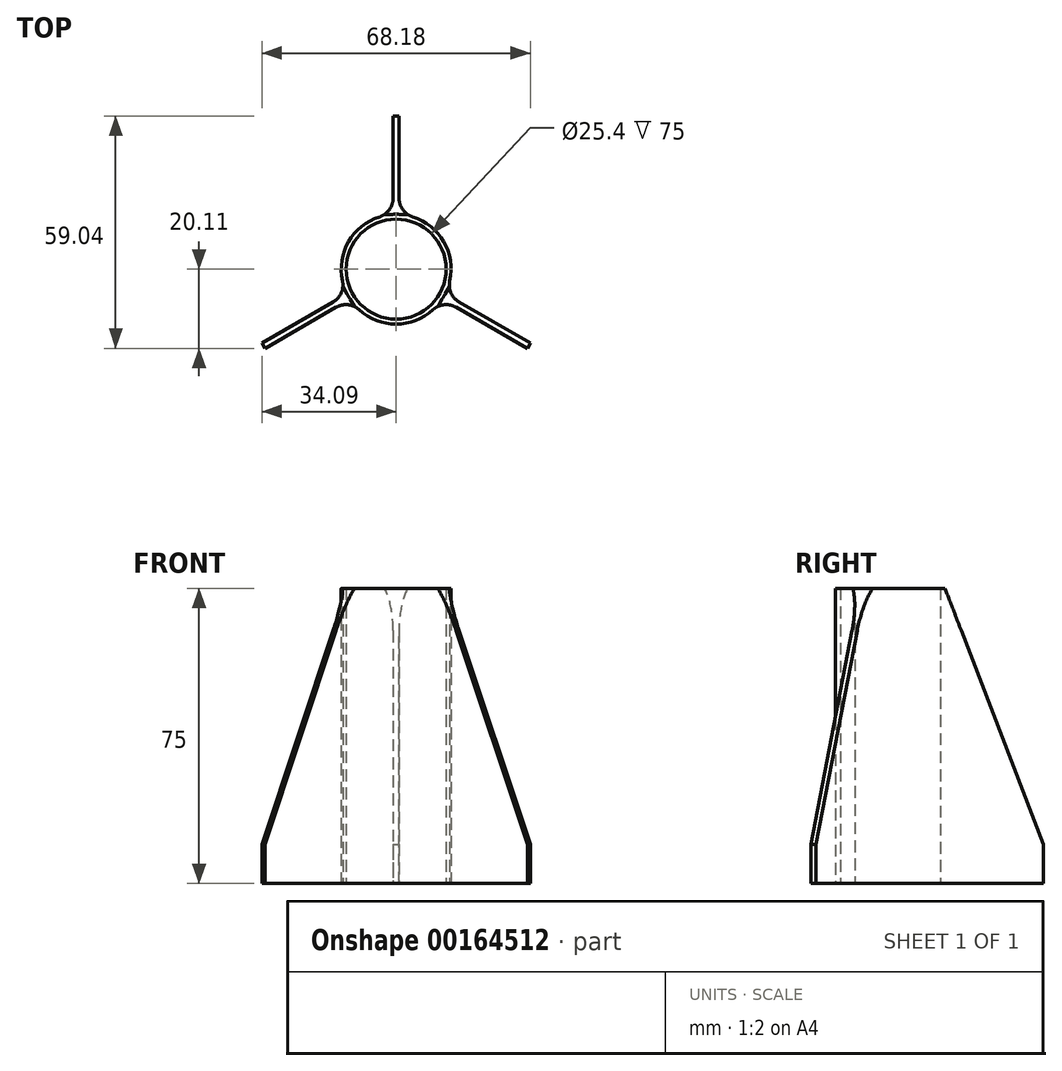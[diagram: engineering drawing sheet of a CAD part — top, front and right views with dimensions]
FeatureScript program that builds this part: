
annotation { "Feature Type Name" : "Feature", "Feature Type Description" : "" }
export const myFeature = defineFeature(function(context is Context, id is Id, definition is map)
    precondition{}
    {
        {
            var Q0;
            Q0=qCreatedBy(makeId("Top.planeOp"),FACE);
            var sketch = newSketch(context, id + "F0", { "sketchPlane" : qUnion([Q0])});
            skCircle(sketch, "E0", {"center": v(0, 0) * mm, "radius": 12.7 * mm});
            skCircle(sketch, "E1", {"center": v(0, 0) * mm, "radius": 13.95 * mm});
            skLineSegment(sketch, "E2", {"start": v(0.75, 13.93) * mm, "end": v(0.75, 38.93) * mm});
            skLineSegment(sketch, "E3", {"start": v(0.75, 38.93) * mm, "end": v(0, 38.93) * mm});
            skLineSegment(sketch, "E4.MirrorCS", {"start": v(-0.75, 13.93) * mm, "end": v(-0.75, 38.93) * mm});
            skLineSegment(sketch, "E5.MirrorCS", {"start": v(-0.75, 38.93) * mm, "end": v(0, 38.93) * mm});
            skSolve(sketch);
        }
        {
            var Q0;
            Q0=makeQuery(id+"F0.imprint","IMPRINT",FACE,{"disambiguationData":[TD([[makeQuery(id+"F0.imprint","IMPRINT",EDGE,{"derivedFrom":sQuery(id+"F0.wireOp",EDGE,"E0")}),-1.0]])]});
            var Q1;
            Q1=makeQuery(id+"F0.imprint","IMPRINT",FACE,{"disambiguationData":[TD([[makeQuery(id+"F0.imprint","IMPRINT",EDGE,{"derivedFrom":sQuery(id+"F0.wireOp",EDGE,"bc061eb7-d542-42eb-8d57-d823a53f24d3.1.0")}),1.0]])]});
            var Q2;
            Q2=makeQuery(id+"F0.imprint","IMPRINT",FACE,{"disambiguationData":[TD([[makeQuery(id+"F0.imprint","IMPRINT",EDGE,{"derivedFrom":sQuery(id+"F0.wireOp",EDGE,"bc061eb7-d542-42eb-8d57-d823a53f24d3.2.0")}),1.0]])]});
            var Q3;
            {var subQ1=sQuery(id+"F0.wireOp",EDGE,"E2");Q3=makeQuery(id+"F0.imprint","IMPRINT",FACE,{"disambiguationData":[TD([[makeQuery(id+"F0.imprint","IMPRINT",EDGE,{"derivedFrom":subQ1}),1.0]])]});}
            extrude(context, id + "F1", {"entities" : qUnion([Q0, Q1, Q2, Q3]), "depth" : 75 * mm});
        }
        {
            var Q0;
            Q0=makeQuery(id+"F1.opExtrude","SWEPT_FACE",FACE,{"disambiguationData":[OSD([sQuery(id+"F0.wireOp",EDGE,"E2")])]});
            var sketch = newSketch(context, id + "F2", { "sketchPlane" : qUnion([Q0])});
            skLineSegment(sketch, "E6.0", {"start": v(13.93, 75) * mm, "end": v(13.93, 0) * mm});
            skLineSegment(sketch, "E7.0", {"start": v(13.93, 0) * mm, "end": v(38.93, 0) * mm});
            skLineSegment(sketch, "E8.0", {"start": v(38.93, 10) * mm, "end": v(38.93, 0) * mm});
            skLineSegment(sketch, "E9", {"start": v(38.93, 10) * mm, "end": v(13.93, 10) * mm});
            skLineSegment(sketch, "E10", {"start": v(13.93, 75) * mm, "end": v(38.93, 10) * mm});
            skPoint(sketch, "E11.orphan", {"position": v(38.93, 75) * mm});
            skSolve(sketch);
        }
        {
            var Q0;
            {var subQ0=sQuery(id+"F2.wireOp",EDGE,"E10");Q0=makeQuery(id+"F2.imprint","IMPRINT",FACE,{"disambiguationData":[TD([[makeQuery(id+"F2.imprint","IMPRINT",EDGE,{"derivedFrom":subQ0}),1.0]])]});}
            extrude(context, id + "F3", {"entities" : qUnion([Q0]), "operationType" : NewBodyOperationType.REMOVE, "endBound" : BoundingType.UP_TO_NEXT, "oppositeDirection" : true, "depth" : 25 * mm});
        }
        {
            var Q0;
            Q0=makeQuery(id+"F1.opExtrude","SWEPT_EDGE",EDGE,{"disambiguationData":[OSD([sQuery(id+"F0.wireOp",EDGE,"E1"),sQuery(id+"F0.wireOp",EDGE,"E2")])]});
            var Q1;
            Q1=makeQuery(id+"F1.opExtrude","SWEPT_EDGE",EDGE,{"disambiguationData":[OSD([sQuery(id+"F0.wireOp",EDGE,"E1"),sQuery(id+"F0.wireOp",EDGE,"E4.MirrorCS")])]});
            fillet(context, id + "F4", {"entities" : qUnion([Q0, Q1]), "radius" : 5 * mm, "tangentPropagation" : true, "allowEdgeOverflow" : false});
        }
        {
            var Q0;
            Q0=qCreatedBy(makeId("Front.planeOp"),FACE);
            var sketch = newSketch(context, id + "F5", { "sketchPlane" : qUnion([Q0])});
            skLineSegment(sketch, "E12", {"start": v(0, 0) * mm, "end": v(0, 85.43) * mm, "construction": true});
            skSolve(sketch);
        }
        {
            var Q0;
            Q0=makeQuery(id+"F1.opExtrude","SWEPT_BODY",BODY,{"disambiguationData":[OSD([sQuery(id+"F0.wireOp",EDGE,"E0"),sQuery(id+"F0.wireOp",EDGE,"E1"),sQuery(id+"F0.wireOp",EDGE,"E2"),sQuery(id+"F0.wireOp",EDGE,"E3"),sQuery(id+"F0.wireOp",EDGE,"E4.MirrorCS"),sQuery(id+"F0.wireOp",EDGE,"E5.MirrorCS")])]});
            var Q1;
            Q1=sQuery(id+"F5.wireOp",EDGE,"E12");
            circularPattern(context, id + "F6", {"operationType" : NewBodyOperationType.ADD, "entities" : qUnion([Q0]), "axis" : qUnion([Q1]), "angle" : 120 * degree, "instanceCount" : 3});
        }
    });
